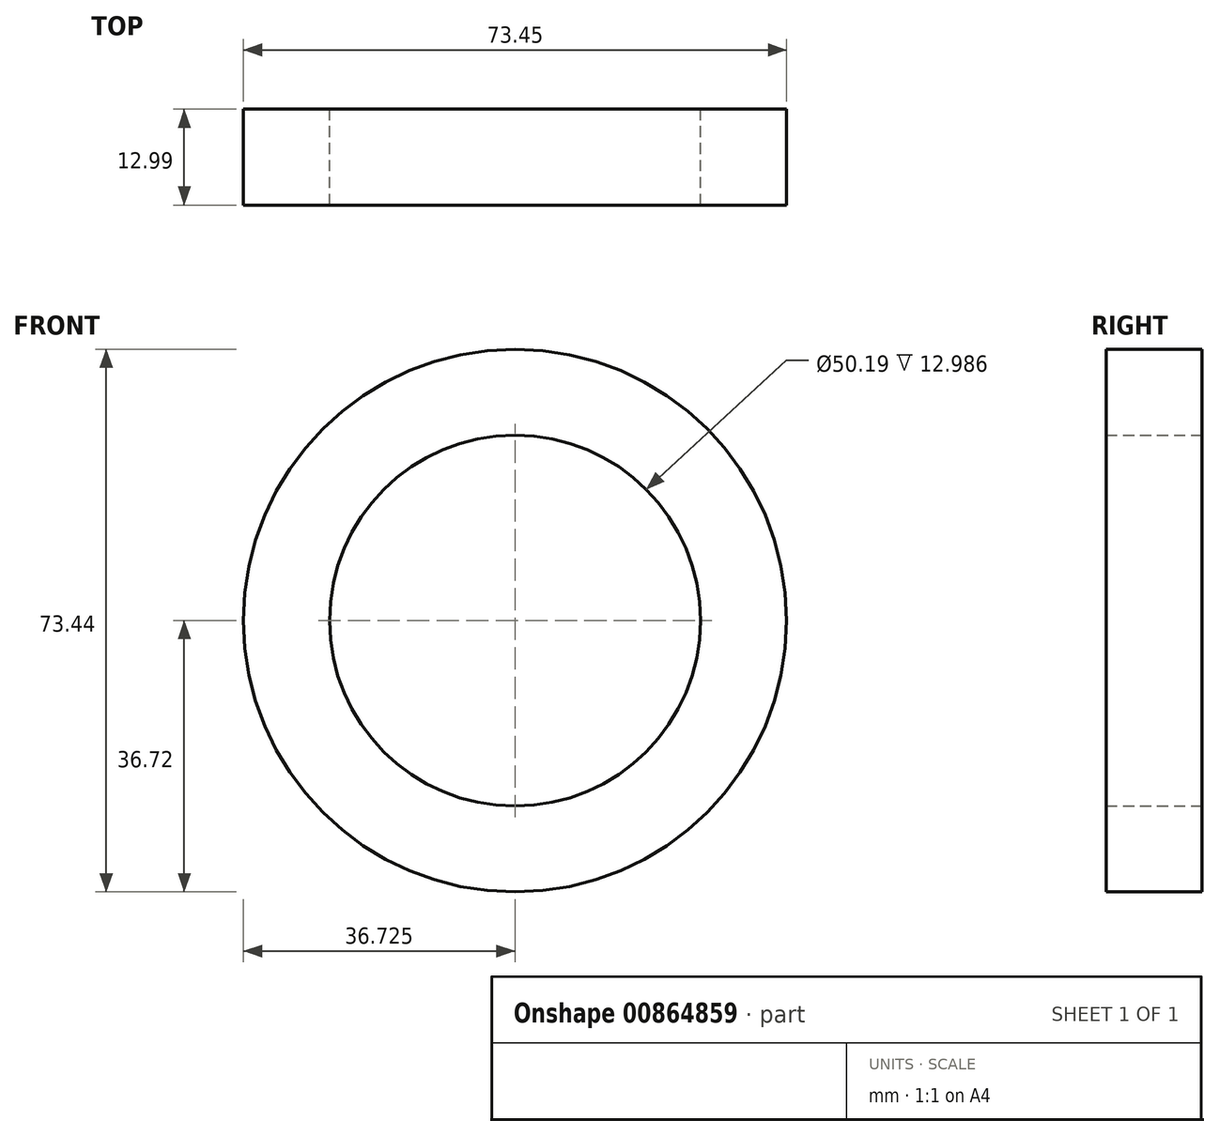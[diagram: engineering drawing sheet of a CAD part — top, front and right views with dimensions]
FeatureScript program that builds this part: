
annotation { "Feature Type Name" : "Feature", "Feature Type Description" : "" }
export const myFeature = defineFeature(function(context is Context, id is Id, definition is map)
    precondition{}
    {
        {
            var Q0;
            Q0=qCreatedBy(makeId("Front.planeOp"),FACE);
            var sketch = newSketch(context, id + "F0", { "sketchPlane" : qUnion([Q0])});
            skCircle(sketch, "E0", {"center": v(27.21, 0) * mm, "radius": 36.72 * mm});
            skCircle(sketch, "E1", {"center": v(27.21, 0) * mm, "radius": 3.92 * mm});
            skCircle(sketch, "E2", {"center": v(27.21, 0) * mm, "radius": 25.1 * mm});
            skCircle(sketch, "E3", {"center": v(27.21, 0) * mm, "radius": 3.87 * mm});
            skSolve(sketch);
        }
        {
            var Q0;
            Q0=makeQuery(id+"F0.imprint","IMPRINT",FACE,{"disambiguationData":[TD([[makeQuery(id+"F0.imprint","IMPRINT",EDGE,{"derivedFrom":sQuery(id+"F0.wireOp",EDGE,"E0")}),1.0]])]});
            extrude(context, id + "F1", {"entities" : qUnion([Q0]), "depth" : 13 * mm, "offsetDistance" : 25.4 * mm});
        }
    });
